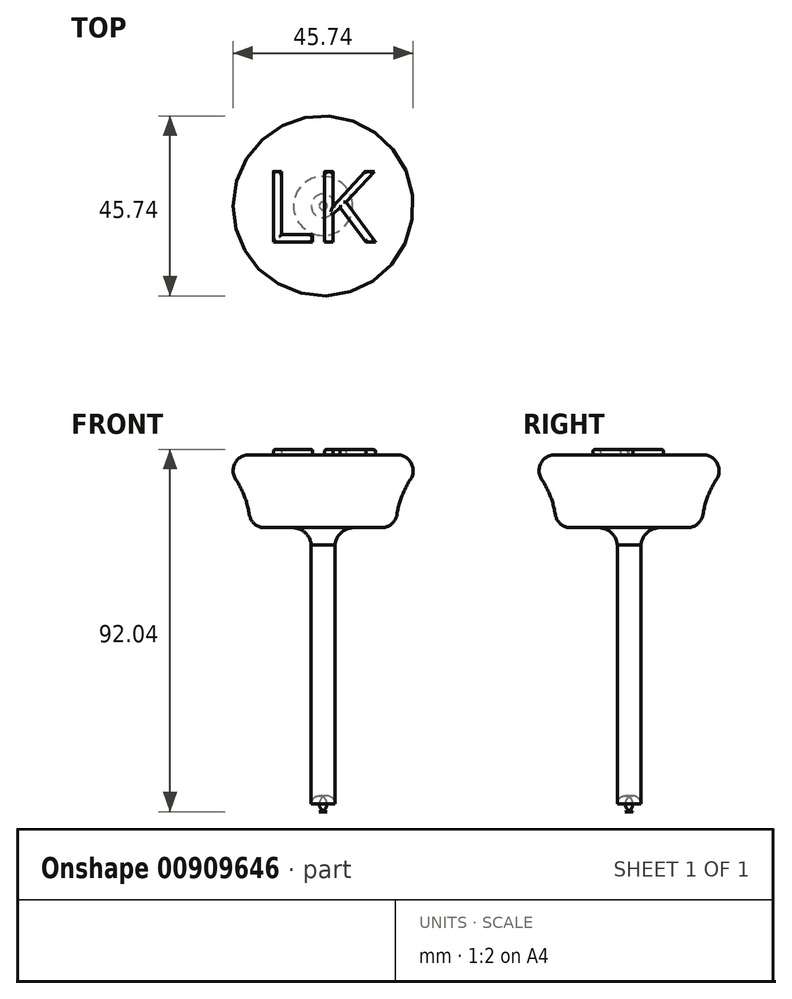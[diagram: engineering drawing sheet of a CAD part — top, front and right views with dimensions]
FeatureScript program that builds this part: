
annotation { "Feature Type Name" : "Feature", "Feature Type Description" : "" }
export const myFeature = defineFeature(function(context is Context, id is Id, definition is map)
    precondition{}
    {
        {
            var Q0;
            Q0=qCreatedBy(makeId("Front.planeOp"),FACE);
            var sketch = newSketch(context, id + "F0", { "sketchPlane" : qUnion([Q0])});
            skLineSegment(sketch, "E0.bottom", {"start": v(3.01, 0) * mm, "end": v(18.5, 0) * mm});
            skLineSegment(sketch, "E0.top", {"start": v(0, 18.5) * mm, "end": v(18.5, 18.5) * mm});
            skLineSegment(sketch, "E0.left", {"start": v(0, 0) * mm, "end": v(0, 18.5) * mm});
            skLineSegment(sketch, "E0.right", {"start": v(18.5, 0) * mm, "end": v(18.5, 18.5) * mm});
            skLineSegment(sketch, "E1.top", {"start": v(0, -72.14) * mm, "end": v(3.01, -72.14) * mm});
            skLineSegment(sketch, "E1.left", {"start": v(0, 0) * mm, "end": v(0, -72.14) * mm});
            skLineSegment(sketch, "E1.right", {"start": v(3.01, 0) * mm, "end": v(3.01, -72.14) * mm});
            skLineSegment(sketch, "E2", {"start": v(0, 28.15) * mm, "end": v(0, -75.22) * mm});
            skArc(sketch, "E3", {"start": v(8.17, 0) * mm, "mid": v(4.71, -1.13) * mm, "end": v(3.01, -4.35) * mm});
            skArc(sketch, "E4", {"start": v(28.32, 18.45) * mm, "mid": v(21.1, 10.45) * mm, "end": v(18.5, 0) * mm});
            skLineSegment(sketch, "E5", {"start": v(18.5, 18.5) * mm, "end": v(28.32, 18.45) * mm});
            skSolve(sketch);
        }
        {
            var Q0;
            Q0 = qSketchRegion(id + "F0", true);
            var Q1;
            Q1=sQuery(id+"F0.wireOp",EDGE,"E2");
            revolve(context, id + "F1", {"surfaceOperationType" : NewSurfaceOperationType.NEW, "entities" : qUnion([Q0]), "axis" : qUnion([Q1]), "revolveType" : RevolveType.FULL});
        }
        {
            var Q0;
            Q0=qCreatedBy(makeId("Top.planeOp"),FACE);
            var sketch = newSketch(context, id + "F2", { "sketchPlane" : qUnion([Q0])});
            skText(sketch, "E6", { "text": "LK", "fontName": "OpenSans-Regular.ttf"});
            const initialGuessF2  = {"E6": [-0.01507, -0.00915, 1, 0, 0.01804]};
            skSetInitialGuess(sketch, initialGuessF2);
            skSolve(sketch);
        }
        {
            var Q0;
            Q0 = qSketchRegion(id + "F2", true);
            extrude(context, id + "F3", {"entities" : qUnion([Q0]), "operationType" : NewBodyOperationType.ADD, "depth" : 19.9 * mm, "offsetDistance" : 25 * mm});
        }
        {
            var Q0;
            Q0=makeQuery(id+"F1.opRevolve","SWEPT_EDGE",EDGE,{"disambiguationData":[OSD([sQuery(id+"F0.wireOp",EDGE,"E0.bottom"),sQuery(id+"F0.wireOp",EDGE,"E0.right"),sQuery(id+"F0.wireOp",EDGE,"E4")])]});
            var Q1;
            Q1=makeQuery(id+"F1.opRevolve","SWEPT_EDGE",EDGE,{"disambiguationData":[OSD([sQuery(id+"F0.wireOp",EDGE,"E4"),sQuery(id+"F0.wireOp",EDGE,"E5")])]});
            fillet(context, id + "F4", {"entities" : qUnion([Q0, Q1]), "radius" : 4 * mm, "tangentPropagation" : true, "allowEdgeOverflow" : false});
        }
        {
            var Q0;
            Q0=makeQuery(id+"F1.opRevolve","SWEPT_EDGE",EDGE,{"disambiguationData":[OSD([sQuery(id+"F0.wireOp",EDGE,"E1.top"),sQuery(id+"F0.wireOp",EDGE,"E1.right")])]});
            fillet(context, id + "F5", {"entities" : qUnion([Q0]), "radius" : 2 * mm, "tangentPropagation" : true, "allowEdgeOverflow" : false});
        }
        {
            var Q0;
            Q0=makeQuery(id+"F3.opExtrude","CAP_EDGE",EDGE,{"disambiguationData":[OSD([sQuery(id+"F2.wireOp",EDGE,"E6.sketch_text.stroke-5")])],"isStart":false});
            var Q1;
            Q1=makeQuery(id+"F3.opExtrude","CAP_EDGE",EDGE,{"disambiguationData":[OSD([sQuery(id+"F2.wireOp",EDGE,"E6.sketch_text.stroke-0")])],"isStart":false});
            var Q2;
            Q2=makeQuery(id+"F3.opExtrude","CAP_EDGE",EDGE,{"disambiguationData":[OSD([sQuery(id+"F2.wireOp",EDGE,"E6.sketch_text.stroke-2")])],"isStart":false});
            var Q3;
            Q3=makeQuery(id+"F3.opExtrude","CAP_EDGE",EDGE,{"disambiguationData":[OSD([sQuery(id+"F2.wireOp",EDGE,"E6.sketch_text.stroke-4")])],"isStart":false});
            var Q4;
            Q4=makeQuery(id+"F3.opExtrude","CAP_EDGE",EDGE,{"disambiguationData":[OSD([sQuery(id+"F2.wireOp",EDGE,"E6.sketch_text.stroke-3")])],"isStart":false});
            var Q5;
            Q5=makeQuery(id+"F3.opExtrude","CAP_EDGE",EDGE,{"disambiguationData":[OSD([sQuery(id+"F2.wireOp",EDGE,"E6.sketch_text.stroke-1")])],"isStart":false});
            var Q6;
            Q6=makeQuery(id+"F3.opExtrude","CAP_EDGE",EDGE,{"disambiguationData":[OSD([sQuery(id+"F2.wireOp",EDGE,"E6.sketch_text.stroke-12")])],"isStart":false});
            var Q7;
            Q7=makeQuery(id+"F3.opExtrude","CAP_EDGE",EDGE,{"disambiguationData":[OSD([sQuery(id+"F2.wireOp",EDGE,"E6.sketch_text.stroke-13")])],"isStart":false});
            var Q8;
            Q8=makeQuery(id+"F3.opExtrude","CAP_EDGE",EDGE,{"disambiguationData":[OSD([sQuery(id+"F2.wireOp",EDGE,"E6.sketch_text.stroke-11")])],"isStart":false});
            var Q9;
            Q9=makeQuery(id+"F3.opExtrude","CAP_EDGE",EDGE,{"disambiguationData":[OSD([sQuery(id+"F2.wireOp",EDGE,"E6.sketch_text.stroke-9")])],"isStart":false});
            var Q10;
            Q10=makeQuery(id+"F3.opExtrude","CAP_EDGE",EDGE,{"disambiguationData":[OSD([sQuery(id+"F2.wireOp",EDGE,"E6.sketch_text.stroke-10")])],"isStart":false});
            var Q11;
            Q11=makeQuery(id+"F3.opExtrude","CAP_EDGE",EDGE,{"disambiguationData":[OSD([sQuery(id+"F2.wireOp",EDGE,"E6.sketch_text.stroke-8")])],"isStart":false});
            var Q12;
            Q12=makeQuery(id+"F3.opExtrude","CAP_EDGE",EDGE,{"disambiguationData":[OSD([sQuery(id+"F2.wireOp",EDGE,"E6.sketch_text.stroke-14")])],"isStart":false});
            var Q13;
            Q13=makeQuery(id+"F3.opExtrude","CAP_EDGE",EDGE,{"disambiguationData":[OSD([sQuery(id+"F2.wireOp",EDGE,"E6.sketch_text.stroke-15")])],"isStart":false});
            var Q14;
            Q14=makeQuery(id+"F3.opExtrude","CAP_EDGE",EDGE,{"disambiguationData":[OSD([sQuery(id+"F2.wireOp",EDGE,"E6.sketch_text.stroke-16")])],"isStart":false});
            var Q15;
            Q15=makeQuery(id+"F3.opExtrude","CAP_EDGE",EDGE,{"disambiguationData":[OSD([sQuery(id+"F2.wireOp",EDGE,"E6.sketch_text.stroke-17")])],"isStart":false});
            var Q16;
            Q16=makeQuery(id+"F3.opExtrude","CAP_EDGE",EDGE,{"disambiguationData":[OSD([sQuery(id+"F2.wireOp",EDGE,"E6.sketch_text.stroke-6")])],"isStart":false});
            var Q17;
            Q17=makeQuery(id+"F3.opExtrude","CAP_EDGE",EDGE,{"disambiguationData":[OSD([sQuery(id+"F2.wireOp",EDGE,"E6.sketch_text.stroke-7")])],"isStart":false});
            fillet(context, id + "F6", {"entities" : qUnion([Q0, Q1, Q2, Q3, Q4, Q5, Q6, Q7, Q8, Q9, Q10, Q11, Q12, Q13, Q14, Q15, Q16, Q17]), "radius" : 0.5 * mm, "tangentPropagation" : true, "allowEdgeOverflow" : false});
        }
    });
